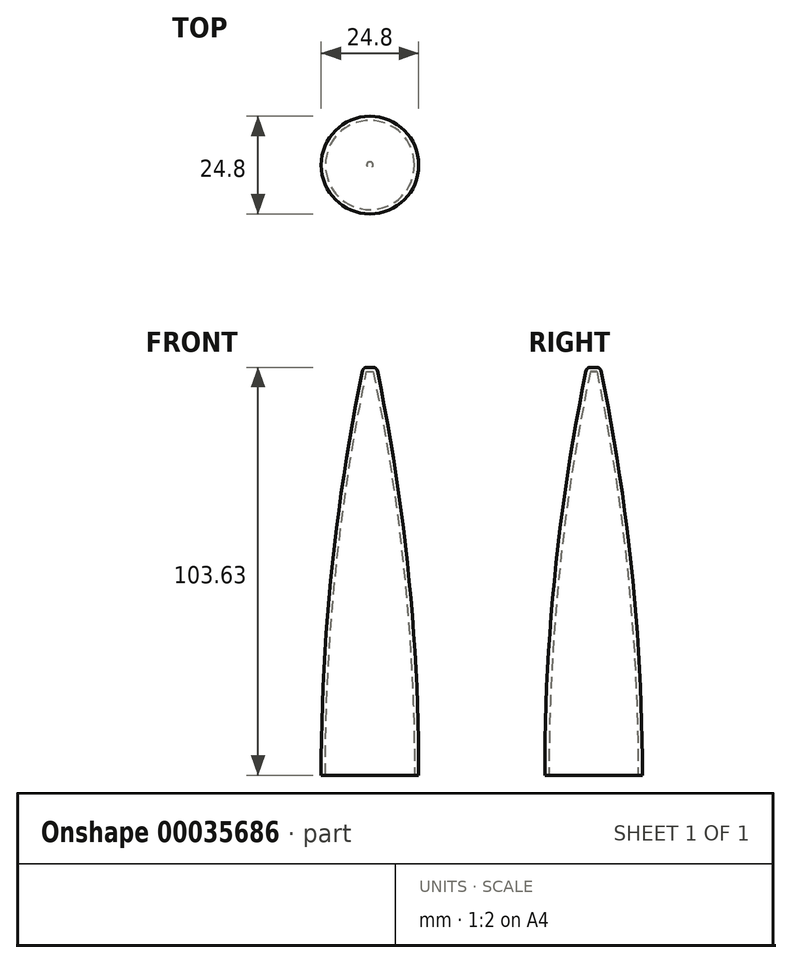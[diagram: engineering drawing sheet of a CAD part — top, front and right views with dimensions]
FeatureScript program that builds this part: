
annotation { "Feature Type Name" : "Feature", "Feature Type Description" : "" }
export const myFeature = defineFeature(function(context is Context, id is Id, definition is map)
    precondition{}
    {
        {
            var Q0;
            Q0=qCreatedBy(makeId("Front.planeOp"),FACE);
            var sketch = newSketch(context, id + "F0", { "sketchPlane" : qUnion([Q0])});
            skLineSegment(sketch, "E0", {"start": v(0, 0) * mm, "end": v(0, 103.63) * mm});
            skLineSegment(sketch, "E1", {"start": v(0, 0) * mm, "end": v(12.4, 0) * mm});
            skArc(sketch, "E2", {"start": v(12.4, 0) * mm, "mid": v(9.76, 51.67) * mm, "end": v(1.87, 102.8) * mm});
            skArc(sketch, "E3", {"start": v(1.87, 102.8) * mm, "mid": v(1.5, 103.4) * mm, "end": v(0.84, 103.63) * mm});
            skLineSegment(sketch, "E4", {"start": v(0, 103.63) * mm, "end": v(0.84, 103.63) * mm});
            skLineSegment(sketch, "E5", {"start": v(-494.7, 0) * mm, "end": v(0, 0) * mm, "construction": true});
            skArc(sketch, "E6", {"start": v(11.32, 0) * mm, "mid": v(8.68, 51.54) * mm, "end": v(0.82, 102.54) * mm});
            skLineSegment(sketch, "E7", {"start": v(0, 102.54) * mm, "end": v(0.82, 102.54) * mm});
            skLineSegment(sketch, "E8", {"start": v(0, 103.63) * mm, "end": v(0, 111.43) * mm, "construction": true});
            skArc(sketch, "E9", {"start": v(1.87, 102.8) * mm, "mid": v(0.95, 107.12) * mm, "end": v(0, 111.43) * mm, "construction": true});
            skSolve(sketch);
        }
        {
            var Q0;
            {var subQ3=sQuery(id+"F0.wireOp",EDGE,"E2");Q0=makeQuery(id+"F0.imprint","IMPRINT",FACE,{"disambiguationData":[TD([[makeQuery(id+"F0.imprint","IMPRINT",EDGE,{"derivedFrom":subQ3}),1.0]])]});}
            var Q1;
            Q1=sQuery(id+"F0.wireOp",EDGE,"E0");
            revolve(context, id + "F1", {"entities" : qUnion([Q0]), "axis" : qUnion([Q1]), "revolveType" : RevolveType.FULL});
        }
    });
